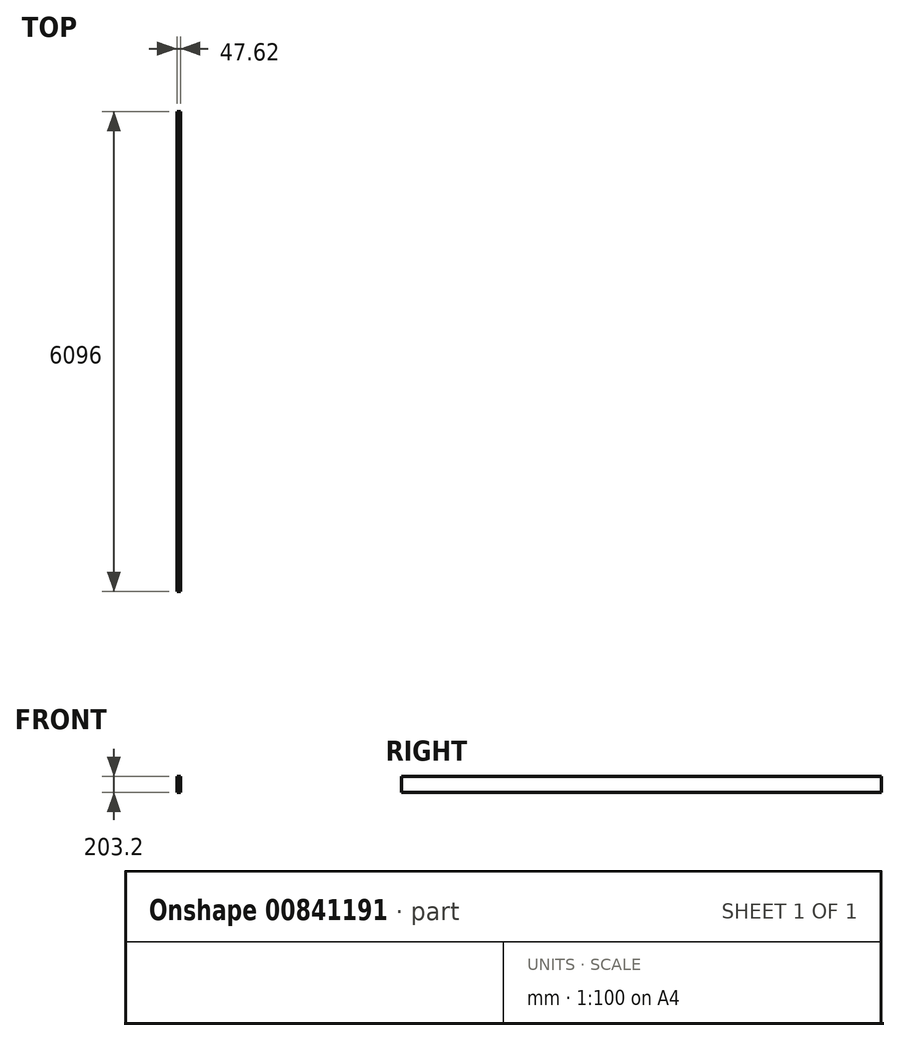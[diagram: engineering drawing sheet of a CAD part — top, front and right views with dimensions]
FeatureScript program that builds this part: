
annotation { "Feature Type Name" : "Feature", "Feature Type Description" : "" }
export const myFeature = defineFeature(function(context is Context, id is Id, definition is map)
    precondition{}
    {
        {
            var Q0;
            Q0=qCreatedBy(makeId("Right.planeOp"),FACE);
            var sketch = newSketch(context, id + "F0", { "sketchPlane" : qUnion([Q0])});
            skLineSegment(sketch, "E0.bottom", {"start": v(0, 0) * mm, "end": v(-6096, 0) * mm});
            skLineSegment(sketch, "E0.top", {"start": v(0, -203.2) * mm, "end": v(-6096, -203.2) * mm});
            skLineSegment(sketch, "E0.left", {"start": v(0, 0) * mm, "end": v(0, -203.2) * mm});
            skLineSegment(sketch, "E0.right", {"start": v(-6096, 0) * mm, "end": v(-6096, -203.2) * mm});
            skSolve(sketch);
        }
        {
            var Q0;
            Q0=makeQuery(id+"F0.imprint","IMPRINT",FACE,{"disambiguationData":[TD([[makeQuery(id+"F0.imprint","IMPRINT",EDGE,{"derivedFrom":sQuery(id+"F0.wireOp",EDGE,"E0.bottom")}),1.0]])]});
            extrude(context, id + "F1", {"entities" : qUnion([Q0]), "depth" : 47.62 * mm, "offsetDistance" : 25.4 * mm});
        }
    });
